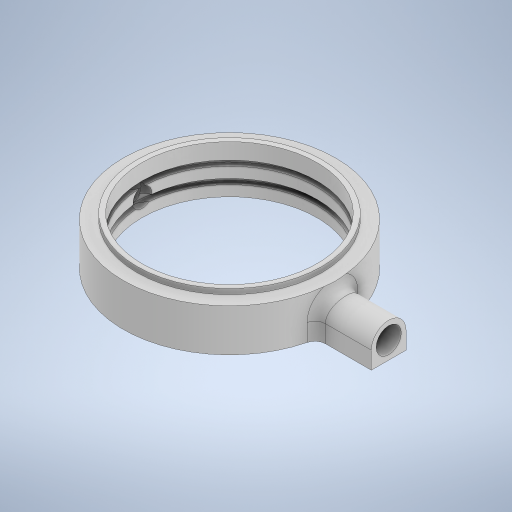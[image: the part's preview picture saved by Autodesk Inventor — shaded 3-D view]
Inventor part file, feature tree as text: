
AUTODESK INVENTOR PART (.ipt)
format: ipt  version: 2023.3 (Build 273359000, 359)  size: 434,176 bytes
history: native  units: mm
features: sketch x4, extrude x4, other x3, draft x2, revolve x1, boolean_combine x1, plane x1, mirror x1, fillet x1
ambient origin geometry x8: Origin, YZ Plane, XZ Plane, XY Plane, X Axis, Y Axis, Z Axis, Center Point
bodies: Solid1 (feature_tree), Solid1_1 (feature_tree)
feature tree (18):
  other  "Sealingring.ipt"
  revolve  "Revolution1"  [1 undecoded]
  boolean_combine  "Combine1"
  plane  "Work Plane1"
  sketch  "Sketch2"  dims[d2=40.0mm d3=360.0deg]
  extrude  "Extrusion1"  TaperAngle=360.0deg  [1 undecoded]
  extrude  "Extrusion2"  Depth=10.0mm
  mirror  "Mirror1"
  extrude  "Extrusion3"  Depth=10.0mm
  draft  "FaceDraft1"
  draft  "FaceDraft2"
  extrude  "Extrusion4"  Depth=10.0mm
  fillet  "Fillet2"  Radius=5.0mm
  sketch  "Sketch1"  dims[d0=33.0mm d1=8.0mm]
  other  "Solid1::Sealingring.ipt"
  other  "TaggingFeature1"
  sketch  "Sketch4"  dims[d4=10.0mm d5=1.0mm]
  sketch  "Sketch5"  dims[d6=34.85mm d7=1.55mm d8=3.490659mm d9=2.91mm d11=5.0mm d12=0.0mm d13=10.0mm d14=0.5mm d15=0.0mm d16=0.0mm d17=0.872665mm d18=0.349066mm d19=2.0mm d21=10.0mm d22=0.0mm d10=0.0mm d20=0.872665mm d23=0.0mm d24=0.0mm d25=0.0mm d26=0.0mm]
note: 2 required parameter values undecoded (feature->parameter linkage not recoverable at this tier; creation-order binding heuristic only, values carry confidence <= 0.55)